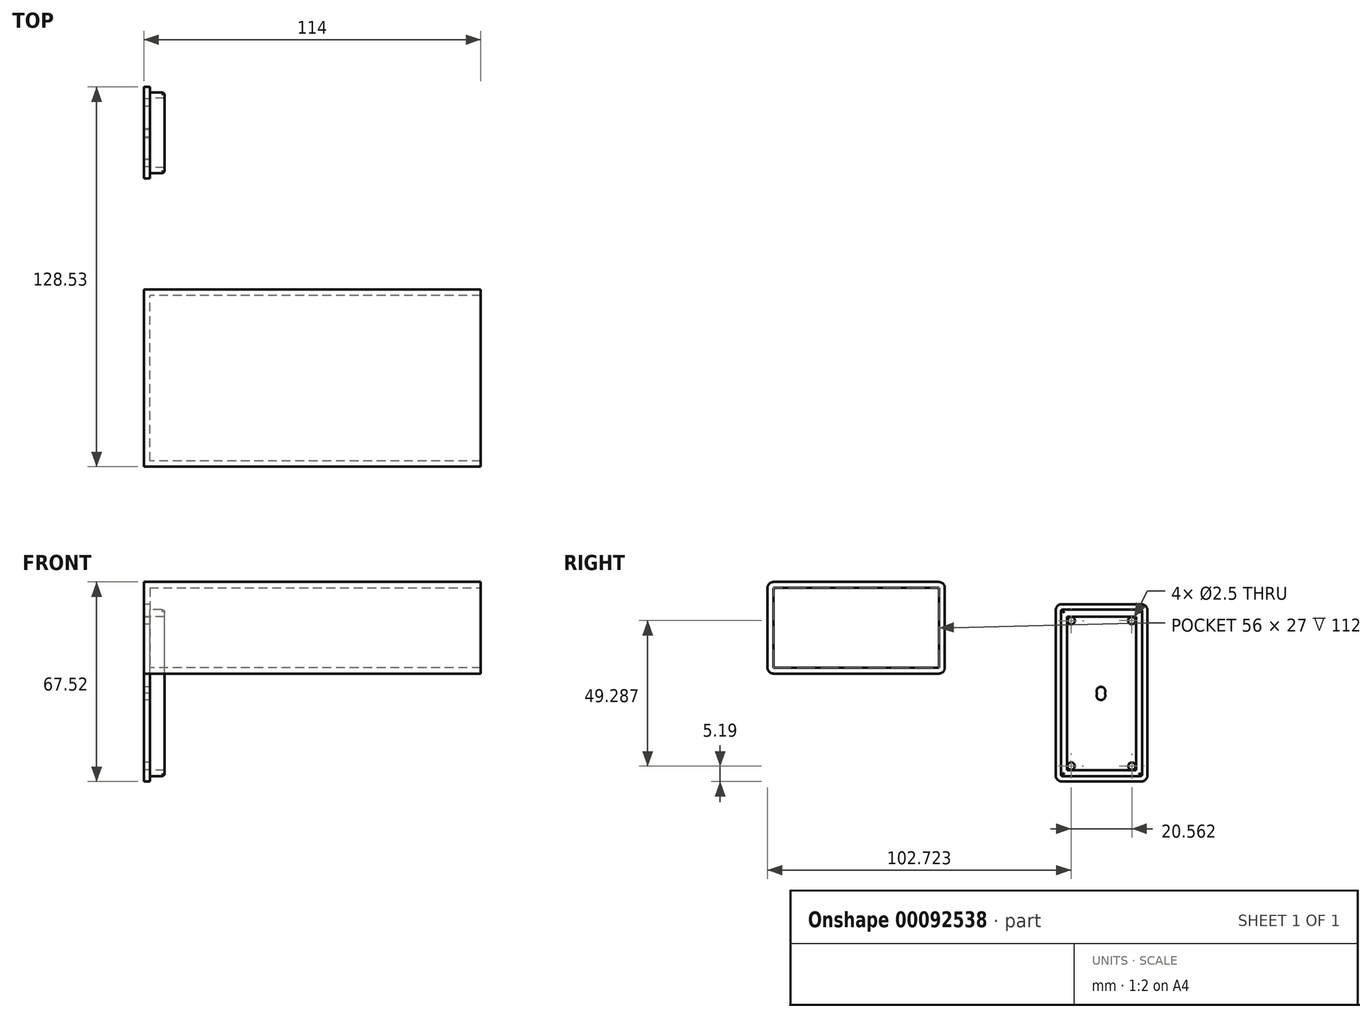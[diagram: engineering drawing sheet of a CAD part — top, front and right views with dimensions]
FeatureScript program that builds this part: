
annotation { "Feature Type Name" : "Feature", "Feature Type Description" : "" }
export const myFeature = defineFeature(function(context is Context, id is Id, definition is map)
    precondition{}
    {
        {
            var Q0;
            Q0=qCreatedBy(makeId("Top.planeOp"),FACE);
            var sketch = newSketch(context, id + "F0", { "sketchPlane" : qUnion([Q0])});
            skLineSegment(sketch, "E0.bottom", {"start": v(0, 0) * mm, "end": v(114, 0) * mm});
            skLineSegment(sketch, "E0.top", {"start": v(0, -60) * mm, "end": v(114, -60) * mm});
            skLineSegment(sketch, "E0.left", {"start": v(0, 0) * mm, "end": v(0, -60) * mm});
            skLineSegment(sketch, "E0.right", {"start": v(114, 0) * mm, "end": v(114, -60) * mm});
            skLineSegment(sketch, "E1.bottom", {"start": v(2, -2) * mm, "end": v(112, -2) * mm});
            skLineSegment(sketch, "E1.top", {"start": v(2, -58) * mm, "end": v(112, -58) * mm});
            skLineSegment(sketch, "E1.left", {"start": v(2, -2) * mm, "end": v(2, -58) * mm});
            skLineSegment(sketch, "E1.right", {"start": v(112, -2) * mm, "end": v(112, -58) * mm});
            skLineSegment(sketch, "E2", {"start": v(112, -30) * mm, "end": v(114, -30) * mm});
            skPoint(sketch, "E2.startSnap0", {"position": v(0, -30) * mm});
            skLineSegment(sketch, "E3", {"start": v(57, -60) * mm, "end": v(57, -58) * mm});
            skLineSegment(sketch, "E4", {"start": v(112, -58) * mm, "end": v(112, -60) * mm});
            skLineSegment(sketch, "E5", {"start": v(112, -2) * mm, "end": v(112, 0) * mm});
            skLineSegment(sketch, "E6", {"start": v(112, -2) * mm, "end": v(114, -2) * mm});
            skLineSegment(sketch, "E7", {"start": v(112, -58) * mm, "end": v(114, -58) * mm});
            skSolve(sketch);
        }
        {
            var Q0;
            Q0=makeQuery(id+"F0.imprint","IMPRINT",FACE,{"disambiguationData":[TD([[makeQuery(id+"F0.imprint","IMPRINT",EDGE,{"derivedFrom":sQuery(id+"F0.wireOp",EDGE,"E0.bottom")}),-1.0]])]});
            var Q1;
            {var subQ3=sQuery(id+"F0.wireOp",EDGE,"E3");Q1=makeQuery(id+"F0.imprint","IMPRINT",FACE,{"disambiguationData":[TD([[makeQuery(id+"F0.imprint","IMPRINT",EDGE,{"derivedFrom":subQ3}),1.0]])]});}
            var Q2;
            {var subQ5=sQuery(id+"F0.wireOp",EDGE,"E1.bottom");Q2=makeQuery(id+"F0.imprint","IMPRINT",FACE,{"disambiguationData":[TD([[makeQuery(id+"F0.imprint","IMPRINT",EDGE,{"derivedFrom":subQ5}),-1.0]])]});}
            var Q3;
            {var subQ0=sQuery(id+"F0.wireOp",EDGE,"E3");Q3=makeQuery(id+"F0.imprint","IMPRINT",FACE,{"disambiguationData":[TD([[makeQuery(id+"F0.imprint","IMPRINT",EDGE,{"derivedFrom":subQ0}),-1.0]])]});}
            var Q4;
            {var subQ3=sQuery(id+"F0.wireOp",EDGE,"E4");Q4=makeQuery(id+"F0.imprint","IMPRINT",FACE,{"disambiguationData":[TD([[makeQuery(id+"F0.imprint","IMPRINT",EDGE,{"derivedFrom":subQ3}),1.0]])]});}
            var Q5;
            {var subQ0=sQuery(id+"F0.wireOp",EDGE,"E2");Q5=makeQuery(id+"F0.imprint","IMPRINT",FACE,{"disambiguationData":[TD([[makeQuery(id+"F0.imprint","IMPRINT",EDGE,{"derivedFrom":subQ0}),-1.0]])]});}
            var Q6;
            {var subQ0=sQuery(id+"F0.wireOp",EDGE,"E2");Q6=makeQuery(id+"F0.imprint","IMPRINT",FACE,{"disambiguationData":[TD([[makeQuery(id+"F0.imprint","IMPRINT",EDGE,{"derivedFrom":subQ0}),1.0]])]});}
            extrude(context, id + "F1", {"entities" : qUnion([Q0, Q1, Q2, Q3, Q4, Q5, Q6]), "depth" : 2 * mm});
        }
        {
            var Q0;
            {var subQ0=sQuery(id+"F0.wireOp",EDGE,"E0.left");Q0=makeQuery(id+"F0.imprint","IMPRINT",FACE,{"disambiguationData":[TD([[makeQuery(id+"F0.imprint","IMPRINT",EDGE,{"derivedFrom":subQ0}),1.0]])]});}
            var Q1;
            {var subQ3=sQuery(id+"F0.wireOp",EDGE,"E5");Q1=makeQuery(id+"F0.imprint","IMPRINT",FACE,{"disambiguationData":[TD([[makeQuery(id+"F0.imprint","IMPRINT",EDGE,{"derivedFrom":subQ3}),-1.0]])]});}
            var Q2;
            {var subQ0=sQuery(id+"F0.wireOp",EDGE,"E3");Q2=makeQuery(id+"F0.imprint","IMPRINT",FACE,{"disambiguationData":[TD([[makeQuery(id+"F0.imprint","IMPRINT",EDGE,{"derivedFrom":subQ0}),-1.0]])]});}
            var Q3;
            {var subQ3=sQuery(id+"F0.wireOp",EDGE,"E4");Q3=makeQuery(id+"F0.imprint","IMPRINT",FACE,{"disambiguationData":[TD([[makeQuery(id+"F0.imprint","IMPRINT",EDGE,{"derivedFrom":subQ3}),1.0]])]});}
            extrude(context, id + "F2", {"entities" : qUnion([Q0, Q1, Q2, Q3]), "operationType" : NewBodyOperationType.ADD, "depth" : 29 * mm});
        }
        {
            var Q0;
            Q0=makeQuery(id+"F2.opExtrude","CAP_FACE",FACE,{"disambiguationData":[OSD([sQuery(id+"F0.wireOp",EDGE,"E0.bottom"),sQuery(id+"F0.wireOp",EDGE,"E0.top"),sQuery(id+"F0.wireOp",EDGE,"E0.left"),sQuery(id+"F0.wireOp",EDGE,"E0.right"),sQuery(id+"F0.wireOp",EDGE,"E1.bottom"),sQuery(id+"F0.wireOp",EDGE,"E1.top"),sQuery(id+"F0.wireOp",EDGE,"E1.left"),sQuery(id+"F0.wireOp",EDGE,"E6"),sQuery(id+"F0.wireOp",EDGE,"E7")])],"isStart":false});
            var sketch = newSketch(context, id + "F3", { "sketchPlane" : qUnion([Q0])});
            skLineSegment(sketch, "E8", {"start": v(114, -2) * mm, "end": v(114, -58) * mm});
            skSolve(sketch);
        }
        {
            var Q0;
            Q0=makeQuery(id+"F3.imprint","IMPRINT",FACE,{"disambiguationData":[TD([[makeQuery(id+"F3.imprint","IMPRINT",EDGE,{"derivedFrom":sQuery(id+"F3.wireOp",EDGE,"E8")}),-1.0]])]});
            var Q1;
            {var subQ1=sQuery(id+"F0.wireOp",EDGE,"E0.bottom");Q1=makeQuery(id+"F3.imprint","IMPRINT",FACE,{"disambiguationData":[TD([[makeQuery(id+"F3.imprint","IMPRINT",EDGE,{"derivedFrom":makeQuery(id+"F2.opExtrude","CAP_EDGE",EDGE,{"disambiguationData":[OSD([subQ1])],"isStart":false})}),-1.0]])]});}
            extrude(context, id + "F4", {"entities" : qUnion([Q0, Q1]), "operationType" : NewBodyOperationType.ADD, "depth" : 2 * mm});
        }
        {
            var Q0;
            {var subQ0=sQuery(id+"F0.wireOp",EDGE,"E0.left");Q0=makeQuery(id+"F4.boolean.opBoolean","MERGE",FACE,{"derivedFrom":[makeQuery(id+"F2.boolean.opBoolean","MERGE",FACE,{"derivedFrom":[makeQuery(id+"F1.opExtrude","SWEPT_FACE",FACE,{"disambiguationData":[OSD([subQ0])]}),makeQuery(id+"F2.opExtrude","SWEPT_FACE",FACE,{"disambiguationData":[OSD([subQ0])]})]}),makeQuery(id+"F4.opExtrude","SWEPT_FACE",FACE,{"disambiguationData":[OSD([subQ0])]})]});}
            var sketch = newSketch(context, id + "F5", { "sketchPlane" : qUnion([Q0])});
            skLineSegment(sketch, "E9.bottom", {"start": v(-68.53, -36.52) * mm, "end": v(-37.53, -36.52) * mm});
            skLineSegment(sketch, "E9.top", {"start": v(-68.53, 23.48) * mm, "end": v(-37.53, 23.48) * mm});
            skLineSegment(sketch, "E9.left", {"start": v(-68.53, -36.52) * mm, "end": v(-68.53, 23.48) * mm});
            skLineSegment(sketch, "E9.right", {"start": v(-37.53, -36.52) * mm, "end": v(-37.53, 23.48) * mm});
            skLineSegment(sketch, "E10.bottom", {"start": v(-66.73, -34.72) * mm, "end": v(-39.33, -34.72) * mm});
            skLineSegment(sketch, "E10.top", {"start": v(-66.73, 21.68) * mm, "end": v(-39.33, 21.68) * mm});
            skLineSegment(sketch, "E10.left", {"start": v(-66.73, -34.72) * mm, "end": v(-66.73, 21.68) * mm});
            skLineSegment(sketch, "E10.right", {"start": v(-39.33, -34.72) * mm, "end": v(-39.33, 21.68) * mm});
            skLineSegment(sketch, "E11.bottom", {"start": v(-64.73, -32.72) * mm, "end": v(-41.33, -32.72) * mm});
            skLineSegment(sketch, "E11.top", {"start": v(-64.73, 19.28) * mm, "end": v(-41.33, 19.28) * mm});
            skLineSegment(sketch, "E11.left", {"start": v(-64.73, -32.72) * mm, "end": v(-64.73, 19.28) * mm});
            skLineSegment(sketch, "E11.right", {"start": v(-41.33, -32.72) * mm, "end": v(-41.33, 19.28) * mm});
            skLineSegment(sketch, "E12", {"start": v(-68.53, -6.52) * mm, "end": v(-66.73, -6.52) * mm});
            skLineSegment(sketch, "E13", {"start": v(-66.73, -6.52) * mm, "end": v(-66.73, -17.5) * mm});
            skLineSegment(sketch, "E14", {"start": v(-66.73, -17.5) * mm, "end": v(-64.73, -17.5) * mm});
            skPoint(sketch, "E14.endSnap0", {"position": v(-64.73, -6.72) * mm});
            skLineSegment(sketch, "E15", {"start": v(-60.23, -34.72) * mm, "end": v(-60.23, -32.72) * mm});
            skLineSegment(sketch, "E16", {"start": v(-53.78, -36.52) * mm, "end": v(-53.78, -34.72) * mm});
            skLineSegment(sketch, "E17", {"start": v(-41.33, -32.72) * mm, "end": v(-42.72, -31.29) * mm});
            skLineSegment(sketch, "E18", {"start": v(-64.73, -32.72) * mm, "end": v(-63.29, -31.33) * mm});
            skLineSegment(sketch, "E19", {"start": v(-64.73, 19.28) * mm, "end": v(-63.23, 17.96) * mm});
            skLineSegment(sketch, "E20", {"start": v(-41.33, 19.28) * mm, "end": v(-42.78, 17.91) * mm});
            skCircle(sketch, "E21", {"center": v(-42.78, 17.91) * mm, "radius": 1.25 * mm});
            skCircle(sketch, "E22", {"center": v(-63.23, 17.96) * mm, "radius": 1.25 * mm});
            skCircle(sketch, "E23", {"center": v(-42.72, -31.29) * mm, "radius": 1.25 * mm});
            skCircle(sketch, "E24", {"center": v(-63.29, -31.33) * mm, "radius": 1.25 * mm});
            skLineSegment(sketch, "E25", {"start": v(-52.83, -6.72) * mm, "end": v(-52.83, -5.97) * mm});
            skLineSegment(sketch, "E26", {"start": v(-52.83, -6.72) * mm, "end": v(-52.83, -7.47) * mm});
            skCircle(sketch, "E27", {"center": v(-52.83, -5.97) * mm, "radius": 1.5 * mm});
            skCircle(sketch, "E28", {"center": v(-52.83, -7.47) * mm, "radius": 1.5 * mm});
            skLineSegment(sketch, "E29", {"start": v(-52.83, -6.72) * mm, "end": v(-52.83, 19.28) * mm});
            skPoint(sketch, "E29.endSnap0", {"position": v(-53.03, 19.28) * mm});
            skLineSegment(sketch, "E30", {"start": v(-52.83, -6.72) * mm, "end": v(-41.33, -6.72) * mm});
            skSolve(sketch);
        }
        {
            var Q0;
            {var subQ4=sQuery(id+"F5.wireOp",EDGE,"E9.top");Q0=makeQuery(id+"F5.imprint","IMPRINT",FACE,{"disambiguationData":[TD([[makeQuery(id+"F5.imprint","IMPRINT",EDGE,{"derivedFrom":subQ4}),-1.0]])]});}
            var Q1;
            {var subQ10=sQuery(id+"F5.wireOp",EDGE,"E10.top");Q1=makeQuery(id+"F5.imprint","IMPRINT",FACE,{"disambiguationData":[TD([[makeQuery(id+"F5.imprint","IMPRINT",EDGE,{"derivedFrom":subQ10}),-1.0]])]});}
            var Q2;
            {var subQ4=sQuery(id+"F5.wireOp",EDGE,"E11.top");Q2=makeQuery(id+"F5.imprint","IMPRINT",FACE,{"disambiguationData":[TD([[makeQuery(id+"F5.imprint","IMPRINT",EDGE,{"derivedFrom":subQ4}),-1.0]])]});}
            var Q3;
            {var subQ9=sQuery(id+"F5.wireOp",EDGE,"E12");Q3=makeQuery(id+"F5.imprint","IMPRINT",FACE,{"disambiguationData":[TD([[makeQuery(id+"F5.imprint","IMPRINT",EDGE,{"derivedFrom":subQ9}),-1.0]])]});}
            var Q4;
            {var subQ3=sQuery(id+"F5.wireOp",EDGE,"E14");Q4=makeQuery(id+"F5.imprint","IMPRINT",FACE,{"disambiguationData":[TD([[makeQuery(id+"F5.imprint","IMPRINT",EDGE,{"derivedFrom":subQ3}),-1.0]])]});}
            var Q5;
            Q5=makeQuery(id+"F5.imprint","IMPRINT",FACE,{"disambiguationData":[TD([[makeQuery(id+"F5.imprint","IMPRINT",EDGE,{"derivedFrom":sQuery(id+"F5.wireOp",EDGE,"E22")}),-1.0]])]});
            extrude(context, id + "F6", {"entities" : qUnion([Q0, Q1, Q2, Q3, Q4, Q5]), "oppositeDirection" : true, "depth" : 2 * mm});
        }
        {
            var Q0;
            {var subQ10=sQuery(id+"F5.wireOp",EDGE,"E10.top");Q0=makeQuery(id+"F5.imprint","IMPRINT",FACE,{"disambiguationData":[TD([[makeQuery(id+"F5.imprint","IMPRINT",EDGE,{"derivedFrom":subQ10}),-1.0]])]});}
            var Q1;
            {var subQ3=sQuery(id+"F5.wireOp",EDGE,"E14");Q1=makeQuery(id+"F5.imprint","IMPRINT",FACE,{"disambiguationData":[TD([[makeQuery(id+"F5.imprint","IMPRINT",EDGE,{"derivedFrom":subQ3}),-1.0]])]});}
            extrude(context, id + "F7", {"entities" : qUnion([Q0, Q1]), "operationType" : NewBodyOperationType.ADD, "oppositeDirection" : true, "depth" : 7 * mm});
        }
        {
            var Q0;
            Q0=makeQuery(id+"F4.opExtrude","CAP_EDGE",EDGE,{"disambiguationData":[OSD([sQuery(id+"F0.wireOp",EDGE,"E0.top")])],"isStart":false});
            var Q1;
            Q1=makeQuery(id+"F1.opExtrude","CAP_EDGE",EDGE,{"disambiguationData":[OSD([sQuery(id+"F0.wireOp",EDGE,"E0.top")])],"isStart":true});
            var Q2;
            Q2=makeQuery(id+"F4.opExtrude","CAP_EDGE",EDGE,{"disambiguationData":[OSD([sQuery(id+"F0.wireOp",EDGE,"E0.bottom")])],"isStart":false});
            var Q3;
            Q3=makeQuery(id+"F1.opExtrude","CAP_EDGE",EDGE,{"disambiguationData":[OSD([sQuery(id+"F0.wireOp",EDGE,"E0.bottom")])],"isStart":true});
            fillet(context, id + "F8", {"entities" : qUnion([Q0, Q1, Q2, Q3]), "radius" : 2 * mm, "tangentPropagation" : true, "allowEdgeOverflow" : false});
        }
        {
            var Q0;
            Q0=makeQuery(id+"F6.opExtrude","SWEPT_EDGE",EDGE,{"disambiguationData":[OSD([sQuery(id+"F5.wireOp",EDGE,"E9.top"),sQuery(id+"F5.wireOp",EDGE,"E9.left")])]});
            var Q1;
            Q1=makeQuery(id+"F6.opExtrude","SWEPT_EDGE",EDGE,{"disambiguationData":[OSD([sQuery(id+"F5.wireOp",EDGE,"E9.top"),sQuery(id+"F5.wireOp",EDGE,"E9.right")])]});
            var Q2;
            Q2=makeQuery(id+"F6.opExtrude","SWEPT_EDGE",EDGE,{"disambiguationData":[OSD([sQuery(id+"F5.wireOp",EDGE,"E9.bottom"),sQuery(id+"F5.wireOp",EDGE,"E9.right")])]});
            var Q3;
            Q3=makeQuery(id+"F6.opExtrude","SWEPT_EDGE",EDGE,{"disambiguationData":[OSD([sQuery(id+"F5.wireOp",EDGE,"E9.bottom"),sQuery(id+"F5.wireOp",EDGE,"E9.left")])]});
            fillet(context, id + "F9", {"entities" : qUnion([Q0, Q1, Q2, Q3]), "radius" : 2 * mm, "tangentPropagation" : true, "allowEdgeOverflow" : false});
        }
        {
            var Q0;
            Q0=makeQuery(id+"F7.opExtrude","SWEPT_EDGE",EDGE,{"disambiguationData":[OSD([sQuery(id+"F5.wireOp",EDGE,"E10.top"),sQuery(id+"F5.wireOp",EDGE,"E10.left")])]});
            var Q1;
            Q1=makeQuery(id+"F7.opExtrude","SWEPT_EDGE",EDGE,{"disambiguationData":[OSD([sQuery(id+"F5.wireOp",EDGE,"E10.top"),sQuery(id+"F5.wireOp",EDGE,"E10.right")])]});
            var Q2;
            Q2=makeQuery(id+"F7.opExtrude","SWEPT_EDGE",EDGE,{"disambiguationData":[OSD([sQuery(id+"F5.wireOp",EDGE,"E10.bottom"),sQuery(id+"F5.wireOp",EDGE,"E10.right")])]});
            var Q3;
            Q3=makeQuery(id+"F7.opExtrude","SWEPT_EDGE",EDGE,{"disambiguationData":[OSD([sQuery(id+"F5.wireOp",EDGE,"E10.bottom"),sQuery(id+"F5.wireOp",EDGE,"E10.left")])]});
            fillet(context, id + "F10", {"entities" : qUnion([Q0, Q1, Q2, Q3]), "radius" : .5 * mm, "tangentPropagation" : true, "allowEdgeOverflow" : false});
        }
        {
            var Q0;
            Q0=makeQuery(id+"F7.opExtrude","CAP_EDGE",EDGE,{"disambiguationData":[OSD([sQuery(id+"F5.wireOp",EDGE,"E10.right")])],"isStart":false});
            fillet(context, id + "F11", {"entities" : qUnion([Q0]), "radius" : 1 * mm, "tangentPropagation" : true, "allowEdgeOverflow" : false});
        }
    });
